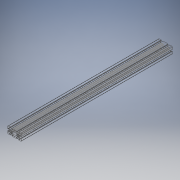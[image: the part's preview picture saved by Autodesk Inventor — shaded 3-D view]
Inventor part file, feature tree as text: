
AUTODESK INVENTOR PART (.ipt)
format: ipt  version: 2019 (Build 230136000, 136)  size: 321,024 bytes
history: native  units: in
note: dims shown in document units (in); Inventor stores cm internally (conversion verified against a paired STEP export)
features: extrude x1, sketch x1
ambient origin geometry x8: Origin, YZ Plane, XZ Plane, XY Plane, X Axis, Y Axis, Z Axis, Center Point
bodies: Solid1 (feature_tree)
feature tree (2):
  extrude  "Extrusion1"  [1 undecoded]
  sketch  "Sketch1"  dims[d0=33.0in d1=0.0in]
note: 1 required parameter value undecoded (feature->parameter linkage not recoverable at this tier; creation-order binding heuristic only, values carry confidence <= 0.55)
